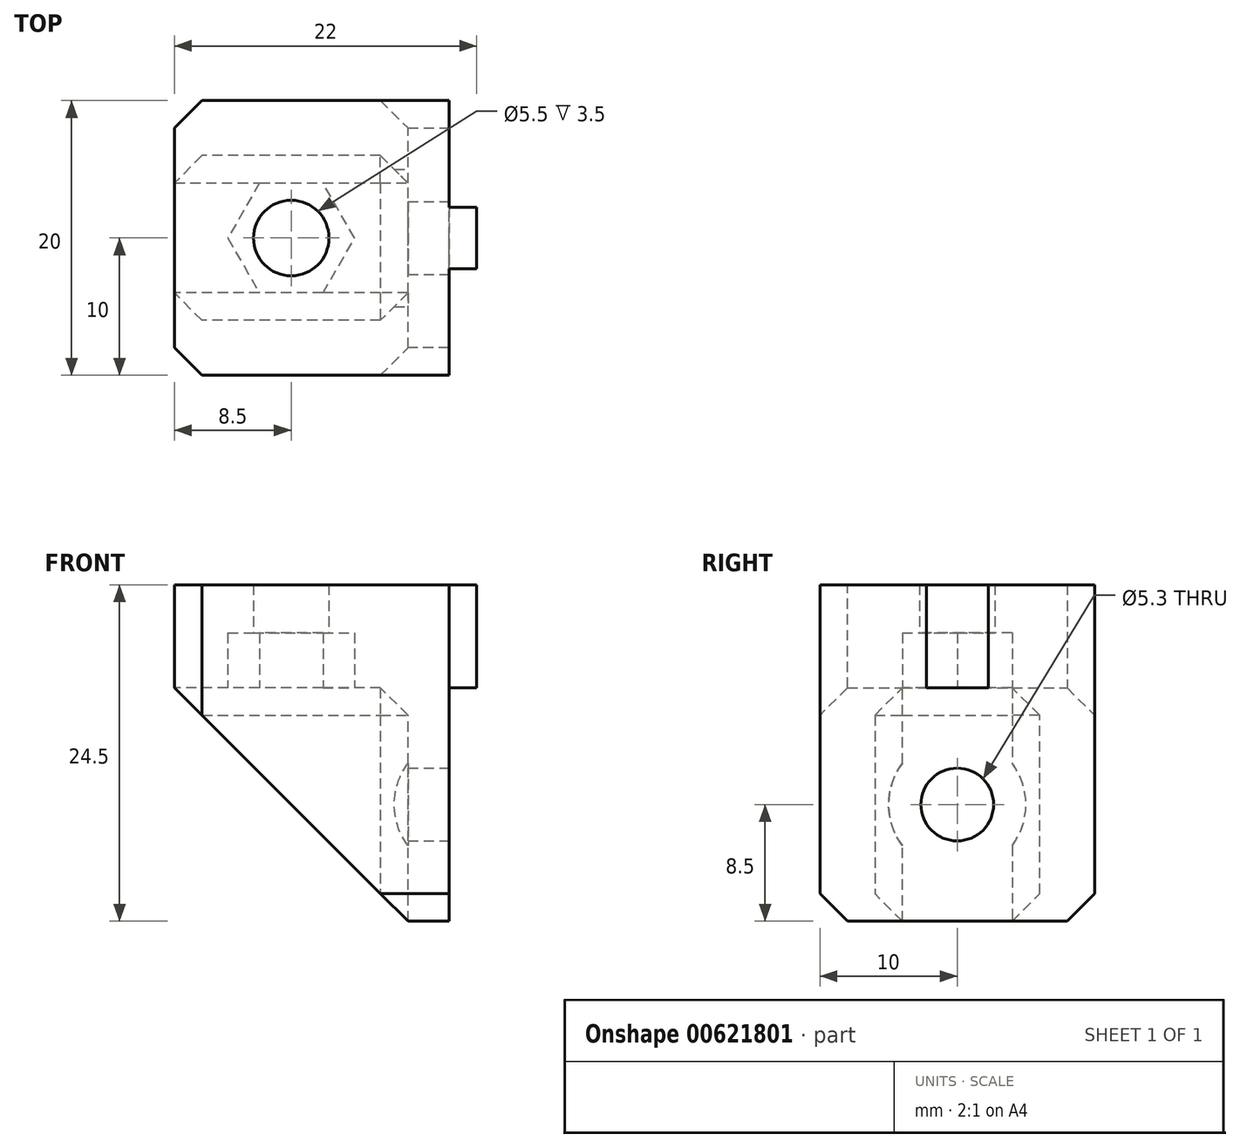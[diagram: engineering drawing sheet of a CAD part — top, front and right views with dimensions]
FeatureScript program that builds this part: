
annotation { "Feature Type Name" : "Feature", "Feature Type Description" : "" }
export const myFeature = defineFeature(function(context is Context, id is Id, definition is map)
    precondition{}
    {
        {
            var Q0;
            Q0=qCreatedBy(makeId("Top.planeOp"),FACE);
            var sketch = newSketch(context, id + "F0", { "sketchPlane" : qUnion([Q0])});
            skLineSegment(sketch, "E0.bottom", {"start": v(10, 10) * mm, "end": v(-10, 10) * mm, "construction": true});
            skLineSegment(sketch, "E0.top", {"start": v(10, -10) * mm, "end": v(-10, -10) * mm, "construction": true});
            skLineSegment(sketch, "E0.left", {"start": v(10, 10) * mm, "end": v(10, -10) * mm, "construction": true});
            skLineSegment(sketch, "E0.right", {"start": v(-10, 10) * mm, "end": v(-10, -10) * mm, "construction": true});
            skPoint(sketch, "E0.middle", {"position": v(0, 0) * mm});
            skLineSegment(sketch, "E1.bottom", {"start": v(-10, 2.25) * mm, "end": v(-8, 2.25) * mm});
            skLineSegment(sketch, "E1.top", {"start": v(-10, -2.25) * mm, "end": v(-8, -2.25) * mm});
            skLineSegment(sketch, "E1.left", {"start": v(-10, 2.25) * mm, "end": v(-10, -2.25) * mm});
            skLineSegment(sketch, "E1.right", {"start": v(-8, 2.25) * mm, "end": v(-8, -2.25) * mm});
            skLineSegment(sketch, "E2", {"start": v(-8, 0) * mm, "end": v(0, 0) * mm, "construction": true});
            skPoint(sketch, "E2.startSnap0", {"position": v(-10, 0) * mm});
            skSolve(sketch);
        }
        {
            var Q0;
            Q0=qSketchRegion(id+"F0",true);
            extrude(context, id + "F1", {"entities" : qUnion([Q0]), "endBound" : BoundingType.SYMMETRIC, "depth" : 15 * mm, "offsetDistance" : 25 * mm});
        }
        {
            var Q0;
            Q0=qCreatedBy(makeId("Front.planeOp"),FACE);
            var sketch = newSketch(context, id + "F2", { "sketchPlane" : qUnion([Q0])});
            skLineSegment(sketch, "E3", {"start": v(-10, 24.5) * mm, "end": v(-10, -24.5) * mm});
            skLineSegment(sketch, "E4", {"start": v(-10, -24.5) * mm, "end": v(-13, -24.5) * mm});
            skLineSegment(sketch, "E5", {"start": v(-13, -24.5) * mm, "end": v(-30, -7.5) * mm});
            skLineSegment(sketch, "E6", {"start": v(-30, -7.5) * mm, "end": v(-30, 7.5) * mm});
            skLineSegment(sketch, "E7", {"start": v(-30, 7.5) * mm, "end": v(-13, 24.5) * mm});
            skLineSegment(sketch, "E8", {"start": v(-13, 24.5) * mm, "end": v(-10, 24.5) * mm});
            skSolve(sketch);
        }
        {
            var Q0;
            Q0=qSketchRegion(id+"F2",true);
            extrude(context, id + "F3", {"entities" : qUnion([Q0]), "operationType" : NewBodyOperationType.ADD, "endBound" : BoundingType.SYMMETRIC, "depth" : 20 * mm, "offsetDistance" : 25 * mm});
        }
        {
            var Q0;
            Q0=qCreatedBy(makeId("Front.planeOp"),FACE);
            var sketch = newSketch(context, id + "F4", { "sketchPlane" : qUnion([Q0])});
            skLineSegment(sketch, "E9", {"start": v(-13, 24.5) * mm, "end": v(-13, 7.5) * mm});
            skLineSegment(sketch, "E10", {"start": v(-13, 7.5) * mm, "end": v(-30, 7.5) * mm});
            skLineSegment(sketch, "E11.0", {"start": v(-30, 7.5) * mm, "end": v(-13, 24.5) * mm});
            skLineSegment(sketch, "E12", {"start": v(-30, -7.5) * mm, "end": v(-13, -7.5) * mm});
            skLineSegment(sketch, "E13", {"start": v(-13, -7.5) * mm, "end": v(-13, -24.5) * mm});
            skLineSegment(sketch, "E14", {"start": v(-13, -24.5) * mm, "end": v(-30, -7.5) * mm});
            skSolve(sketch);
        }
        {
            var Q0;
            Q0=qSketchRegion(id+"F4",true);
            extrude(context, id + "F5", {"entities" : qUnion([Q0]), "operationType" : NewBodyOperationType.REMOVE, "endBound" : BoundingType.SYMMETRIC, "depth" : 12 * mm, "offsetDistance" : 25 * mm});
        }
        {
            var Q0;
            Q0=makeQuery(id+"F5.boolean.opBoolean","COPY",EDGE,{"derivedFrom":makeQuery(id+"F5.opExtrude","CAP_EDGE",EDGE,{"disambiguationData":[OSD([sQuery(id+"F4.wireOp",EDGE,"E13")])],"isStart":true})});
            var Q1;
            Q1=makeQuery(id+"F5.boolean.opBoolean","COPY",EDGE,{"derivedFrom":makeQuery(id+"F5.opExtrude","CAP_EDGE",EDGE,{"disambiguationData":[OSD([sQuery(id+"F4.wireOp",EDGE,"E12")])],"isStart":true})});
            var Q2;
            Q2=makeQuery(id+"F5.boolean.opBoolean","COPY",EDGE,{"derivedFrom":makeQuery(id+"F5.opExtrude","SWEPT_EDGE",EDGE,{"disambiguationData":[OSD([sQuery(id+"F4.wireOp",EDGE,"E12"),sQuery(id+"F4.wireOp",EDGE,"E13")])]})});
            var Q3;
            Q3=makeQuery(id+"F5.boolean.opBoolean","COPY",EDGE,{"derivedFrom":makeQuery(id+"F5.opExtrude","CAP_EDGE",EDGE,{"disambiguationData":[OSD([sQuery(id+"F4.wireOp",EDGE,"E12")])],"isStart":false})});
            var Q4;
            Q4=makeQuery(id+"F5.boolean.opBoolean","COPY",EDGE,{"derivedFrom":makeQuery(id+"F5.opExtrude","CAP_EDGE",EDGE,{"disambiguationData":[OSD([sQuery(id+"F4.wireOp",EDGE,"E13")])],"isStart":false})});
            var Q5;
            Q5=makeQuery(id+"F5.boolean.opBoolean","COPY",EDGE,{"derivedFrom":makeQuery(id+"F5.opExtrude","CAP_EDGE",EDGE,{"disambiguationData":[OSD([sQuery(id+"F4.wireOp",EDGE,"E10")])],"isStart":false})});
            var Q6;
            Q6=makeQuery(id+"F5.boolean.opBoolean","COPY",EDGE,{"derivedFrom":makeQuery(id+"F5.opExtrude","CAP_EDGE",EDGE,{"disambiguationData":[OSD([sQuery(id+"F4.wireOp",EDGE,"E9")])],"isStart":false})});
            var Q7;
            Q7=makeQuery(id+"F5.boolean.opBoolean","COPY",EDGE,{"derivedFrom":makeQuery(id+"F5.opExtrude","CAP_EDGE",EDGE,{"disambiguationData":[OSD([sQuery(id+"F4.wireOp",EDGE,"E9")])],"isStart":true})});
            var Q8;
            Q8=makeQuery(id+"F5.boolean.opBoolean","COPY",EDGE,{"derivedFrom":makeQuery(id+"F5.opExtrude","CAP_EDGE",EDGE,{"disambiguationData":[OSD([sQuery(id+"F4.wireOp",EDGE,"E10")])],"isStart":true})});
            var Q9;
            Q9=makeQuery(id+"F5.boolean.opBoolean","COPY",EDGE,{"derivedFrom":makeQuery(id+"F5.opExtrude","SWEPT_EDGE",EDGE,{"disambiguationData":[OSD([sQuery(id+"F4.wireOp",EDGE,"E9"),sQuery(id+"F4.wireOp",EDGE,"E10")])]})});
            chamfer(context, id + "F6", {"entities" : qUnion([Q0, Q1, Q2, Q3, Q4, Q5, Q6, Q7, Q8, Q9]), "width" : 2 * mm, "tangentPropagation" : true});
        }
        {
            var Q0;
            Q0=makeQuery(id+"F3.opExtrude","CAP_EDGE",EDGE,{"disambiguationData":[OSD([sQuery(id+"F2.wireOp",EDGE,"E6")])],"isStart":false});
            var Q1;
            Q1=makeQuery(id+"F3.opExtrude","CAP_EDGE",EDGE,{"disambiguationData":[OSD([sQuery(id+"F2.wireOp",EDGE,"E6")])],"isStart":true});
            chamfer(context, id + "F7", {"entities" : qUnion([Q0, Q1]), "width" : 2 * mm, "tangentPropagation" : true});
        }
        {
            var Q0;
            Q0=makeQuery(id+"F3.opExtrude","SWEPT_FACE",FACE,{"disambiguationData":[OSD([sQuery(id+"F2.wireOp",EDGE,"E3")])]});
            var sketch = newSketch(context, id + "F8", { "sketchPlane" : qUnion([Q0])});
            skLineSegment(sketch, "E15", {"start": v(0, -24.5) * mm, "end": v(0, -7.5) * mm, "construction": true});
            skLineSegment(sketch, "E16", {"start": v(0, 7.5) * mm, "end": v(0, 24.5) * mm, "construction": true});
            skCircle(sketch, "E17", {"center": v(0, -16) * mm, "radius": 2.65 * mm});
            skCircle(sketch, "E18", {"center": v(0, 16) * mm, "radius": 2.65 * mm});
            skSolve(sketch);
        }
        {
            var Q0;
            Q0=qSketchRegion(id+"F8",true);
            extrude(context, id + "F9", {"entities" : qUnion([Q0]), "operationType" : NewBodyOperationType.REMOVE, "oppositeDirection" : true, "depth" : 25 * mm, "offsetDistance" : 25 * mm});
        }
        {
            var Q0;
            Q0=makeQuery(id+"F3.opExtrude","CAP_EDGE",EDGE,{"disambiguationData":[OSD([sQuery(id+"F2.wireOp",EDGE,"E4")])],"isStart":true});
            var Q1;
            Q1=makeQuery(id+"F3.opExtrude","CAP_EDGE",EDGE,{"disambiguationData":[OSD([sQuery(id+"F2.wireOp",EDGE,"E4")])],"isStart":false});
            var Q2;
            Q2=makeQuery(id+"F3.opExtrude","CAP_EDGE",EDGE,{"disambiguationData":[OSD([sQuery(id+"F2.wireOp",EDGE,"E8")])],"isStart":true});
            var Q3;
            Q3=makeQuery(id+"F3.opExtrude","CAP_EDGE",EDGE,{"disambiguationData":[OSD([sQuery(id+"F2.wireOp",EDGE,"E8")])],"isStart":false});
            chamfer(context, id + "F10", {"entities" : qUnion([Q0, Q1, Q2, Q3]), "width" : 2 * mm, "tangentPropagation" : true});
        }
        {
            var Q0;
            Q0=makeQuery(id+"F5.boolean.opBoolean","COPY",FACE,{"derivedFrom":makeQuery(id+"F5.opExtrude","SWEPT_FACE",FACE,{"disambiguationData":[OSD([sQuery(id+"F4.wireOp",EDGE,"E9")])]})});
            var sketch = newSketch(context, id + "F11", { "sketchPlane" : qUnion([Q0])});
            skCircle(sketch, "E19", {"center": v(0, 16) * mm, "radius": 5 * mm});
            skCircle(sketch, "E20", {"center": v(0, -16) * mm, "radius": 5 * mm});
            skSolve(sketch);
        }
        {
            var Q0;
            Q0=qSketchRegion(id+"F11",true);
            var Q1;
            Q1=sQuery(id+"F11.wireOp",EDGE,"E19");
            extrude(context, id + "F12", {"entities" : qUnion([Q0]), "operationType" : NewBodyOperationType.REMOVE, "surfaceEntities" : qUnion([Q1]), "depth" : 25 * mm, "offsetDistance" : 25 * mm});
        }
        {
            var Q0;
            Q0=makeQuery(id+"F3.opExtrude","CAP_FACE",FACE,{"disambiguationData":[OSD([sQuery(id+"F2.wireOp",EDGE,"E3"),sQuery(id+"F2.wireOp",EDGE,"E4"),sQuery(id+"F2.wireOp",EDGE,"E5"),sQuery(id+"F2.wireOp",EDGE,"E6"),sQuery(id+"F2.wireOp",EDGE,"E7"),sQuery(id+"F2.wireOp",EDGE,"E8")])],"isStart":false});
            var sketch = newSketch(context, id + "F13", { "sketchPlane" : qUnion([Q0])});
            skLineSegment(sketch, "E21.bottom", {"start": v(-30, 24.5) * mm, "end": v(-8, 24.5) * mm});
            skLineSegment(sketch, "E21.top", {"start": v(-30, 0) * mm, "end": v(-8, 0) * mm});
            skLineSegment(sketch, "E21.left", {"start": v(-30, 24.5) * mm, "end": v(-30, 0) * mm});
            skLineSegment(sketch, "E21.right", {"start": v(-8, 24.5) * mm, "end": v(-8, 0) * mm});
            skSolve(sketch);
        }
        {
            var Q0;
            Q0 = qSketchRegion(id + "F13", true);
            extrude(context, id + "F14", {"entities" : qUnion([Q0]), "operationType" : NewBodyOperationType.REMOVE, "oppositeDirection" : true, "depth" : 25 * mm, "offsetDistance" : 25 * mm});
        }
        {
            var Q0;
            Q0=makeQuery(id+"F5.boolean.opBoolean","COPY",FACE,{"derivedFrom":makeQuery(id+"F5.opExtrude","SWEPT_FACE",FACE,{"disambiguationData":[OSD([sQuery(id+"F4.wireOp",EDGE,"E12")])]})});
            var sketch = newSketch(context, id + "F15", { "sketchPlane" : qUnion([Q0])});
            skLineSegment(sketch, "E22", {"start": v(-30, 0) * mm, "end": v(-13, 0) * mm, "construction": true});
            skPoint(sketch, "E22.endSnap0", {"position": v(-30, 0) * mm});
            skCircle(sketch, "E23.cCircle", {"center": v(-21.5, 0) * mm, "radius": 4 * mm, "construction": true});
            skLineSegment(sketch, "E23.0", {"start": v(-23.8, 4) * mm, "end": v(-19.2, 4) * mm});
            skLineSegment(sketch, "E23.1", {"start": v(-19.2, 4) * mm, "end": v(-16.88, 0) * mm});
            skLineSegment(sketch, "E23.2", {"start": v(-16.88, 0) * mm, "end": v(-19.2, -4) * mm});
            skLineSegment(sketch, "E23.3", {"start": v(-19.2, -4) * mm, "end": v(-23.8, -4) * mm});
            skLineSegment(sketch, "E23.4", {"start": v(-23.8, -4) * mm, "end": v(-26.12, 0) * mm});
            skLineSegment(sketch, "E23.5", {"start": v(-26.12, 0) * mm, "end": v(-23.8, 4) * mm});
            skPoint(sketch, "E23.0.midPoint", {"position": v(-21.5, 4) * mm});
            skSolve(sketch);
        }
        {
            var Q0;
            Q0 = qSketchRegion(id + "F15", true);
            extrude(context, id + "F16", {"entities" : qUnion([Q0]), "operationType" : NewBodyOperationType.REMOVE, "oppositeDirection" : true, "depth" : 4 * mm, "offsetDistance" : 25 * mm});
        }
        {
            var Q0;
            Q0=makeQuery(id+"F16.boolean.opBoolean","COPY",FACE,{"derivedFrom":makeQuery(id+"F16.opExtrude","CAP_FACE",FACE,{"disambiguationData":[OSD([sQuery(id+"F15.wireOp",EDGE,"E23.0"),sQuery(id+"F15.wireOp",EDGE,"E23.1"),sQuery(id+"F15.wireOp",EDGE,"E23.2"),sQuery(id+"F15.wireOp",EDGE,"E23.3"),sQuery(id+"F15.wireOp",EDGE,"E23.4"),sQuery(id+"F15.wireOp",EDGE,"E23.5")])],"isStart":false})});
            var sketch = newSketch(context, id + "F17", { "sketchPlane" : qUnion([Q0])});
            skCircle(sketch, "E24", {"center": v(-21.5, 0) * mm, "radius": 2.75 * mm});
            skSolve(sketch);
        }
        {
            var Q0;
            Q0 = qSketchRegion(id + "F17", true);
            extrude(context, id + "F18", {"entities" : qUnion([Q0]), "operationType" : NewBodyOperationType.REMOVE, "oppositeDirection" : true, "depth" : 25 * mm, "offsetDistance" : 25 * mm});
        }
    });
